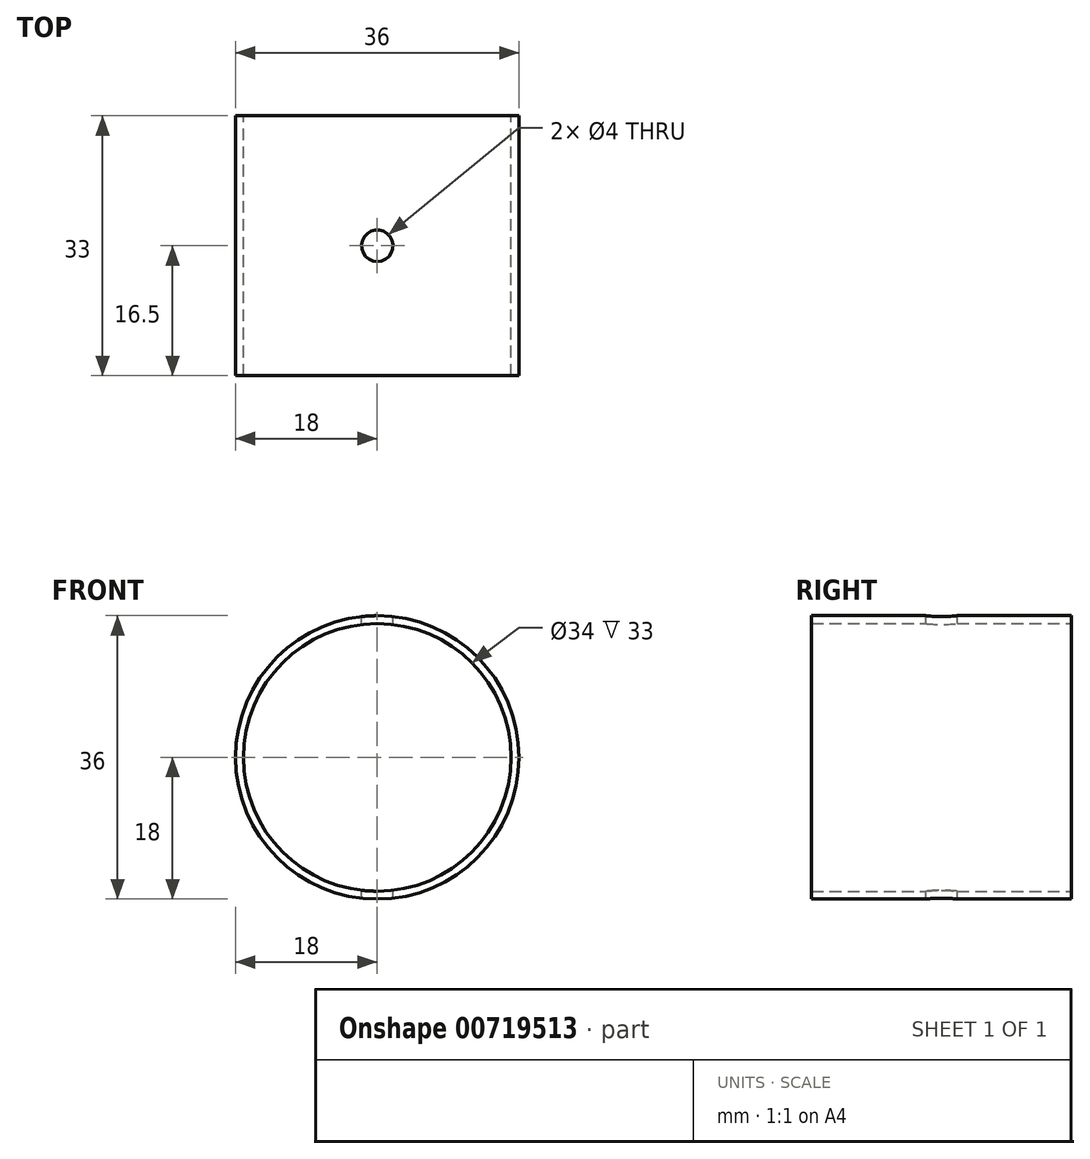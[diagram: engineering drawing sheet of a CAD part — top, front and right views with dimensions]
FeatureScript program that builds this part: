
annotation { "Feature Type Name" : "Feature", "Feature Type Description" : "" }
export const myFeature = defineFeature(function(context is Context, id is Id, definition is map)
    precondition{}
    {
        {
            var Q0;
            Q0=qCreatedBy(makeId("Front.planeOp"),FACE);
            var sketch = newSketch(context, id + "F0", { "sketchPlane" : qUnion([Q0])});
            skCircle(sketch, "E0", {"center": v(0, 0) * mm, "radius": 18 * mm});
            skCircle(sketch, "E1", {"center": v(0, 0) * mm, "radius": 17 * mm});
            skSolve(sketch);
        }
        {
            var Q0;
            Q0=makeQuery(id+"F0.imprint","IMPRINT",FACE,{"disambiguationData":[TD([[makeQuery(id+"F0.imprint","IMPRINT",EDGE,{"derivedFrom":sQuery(id+"F0.wireOp",EDGE,"E0")}),1.0]])]});
            extrude(context, id + "F1", {"entities" : qUnion([Q0]), "endBound" : BoundingType.SYMMETRIC, "depth" : 33 * mm, "offsetDistance" : 25 * mm});
        }
        {
            var Q0;
            Q0=qCreatedBy(makeId("Top.planeOp"),FACE);
            var sketch = newSketch(context, id + "F2", { "sketchPlane" : qUnion([Q0])});
            skCircle(sketch, "E2", {"center": v(0, 0) * mm, "radius": 2 * mm});
            skSolve(sketch);
        }
        {
            var Q0;
            Q0 = qSketchRegion(id + "F2", true);
            extrude(context, id + "F3", {"entities" : qUnion([Q0]), "operationType" : NewBodyOperationType.REMOVE, "endBound" : BoundingType.SYMMETRIC, "oppositeDirection" : true, "depth" : 38 * mm, "offsetDistance" : 25 * mm});
        }
    });
